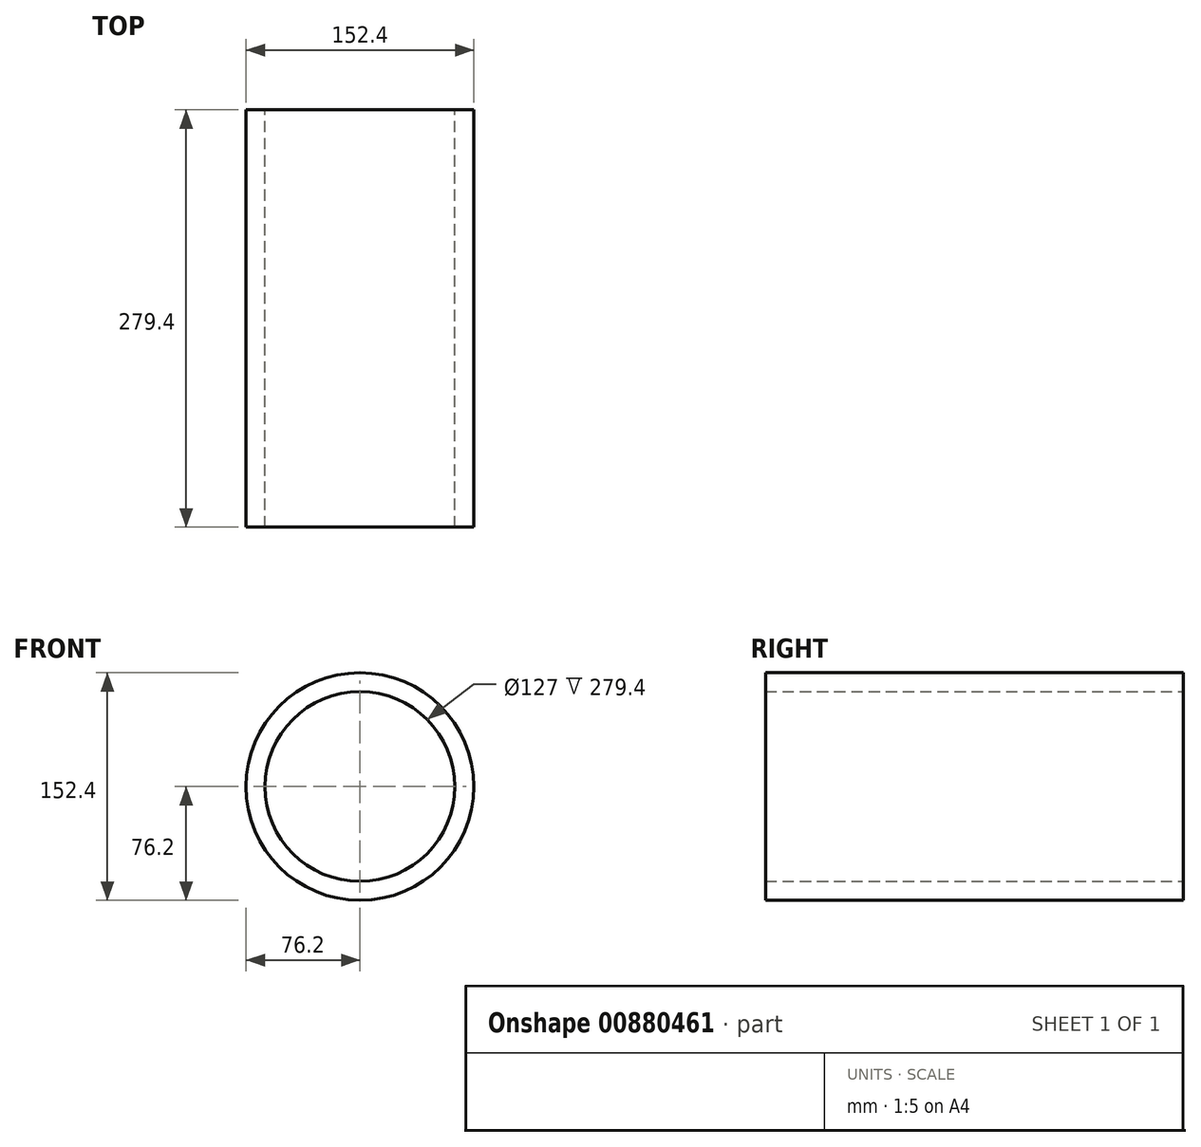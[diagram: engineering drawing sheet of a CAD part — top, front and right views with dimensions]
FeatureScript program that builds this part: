
annotation { "Feature Type Name" : "Feature", "Feature Type Description" : "" }
export const myFeature = defineFeature(function(context is Context, id is Id, definition is map)
    precondition{}
    {
        {
            var Q0;
            Q0=qCreatedBy(makeId("Front.planeOp"),FACE);
            var sketch = newSketch(context, id + "F0", { "sketchPlane" : qUnion([Q0])});
            skCircle(sketch, "E0", {"center": v(0, 0) * mm, "radius": 76.2 * mm});
            skCircle(sketch, "E1", {"center": v(0, 0) * mm, "radius": 63.5 * mm});
            skSolve(sketch);
        }
        {
            var Q0;
            Q0=makeQuery(id+"F0.imprint","IMPRINT",FACE,{"disambiguationData":[TD([[makeQuery(id+"F0.imprint","IMPRINT",EDGE,{"derivedFrom":sQuery(id+"F0.wireOp",EDGE,"E0")}),1.0]])]});
            extrude(context, id + "F1", {"entities" : qUnion([Q0]), "depth" : 279.4 * mm, "offsetDistance" : 25.4 * mm});
        }
    });
